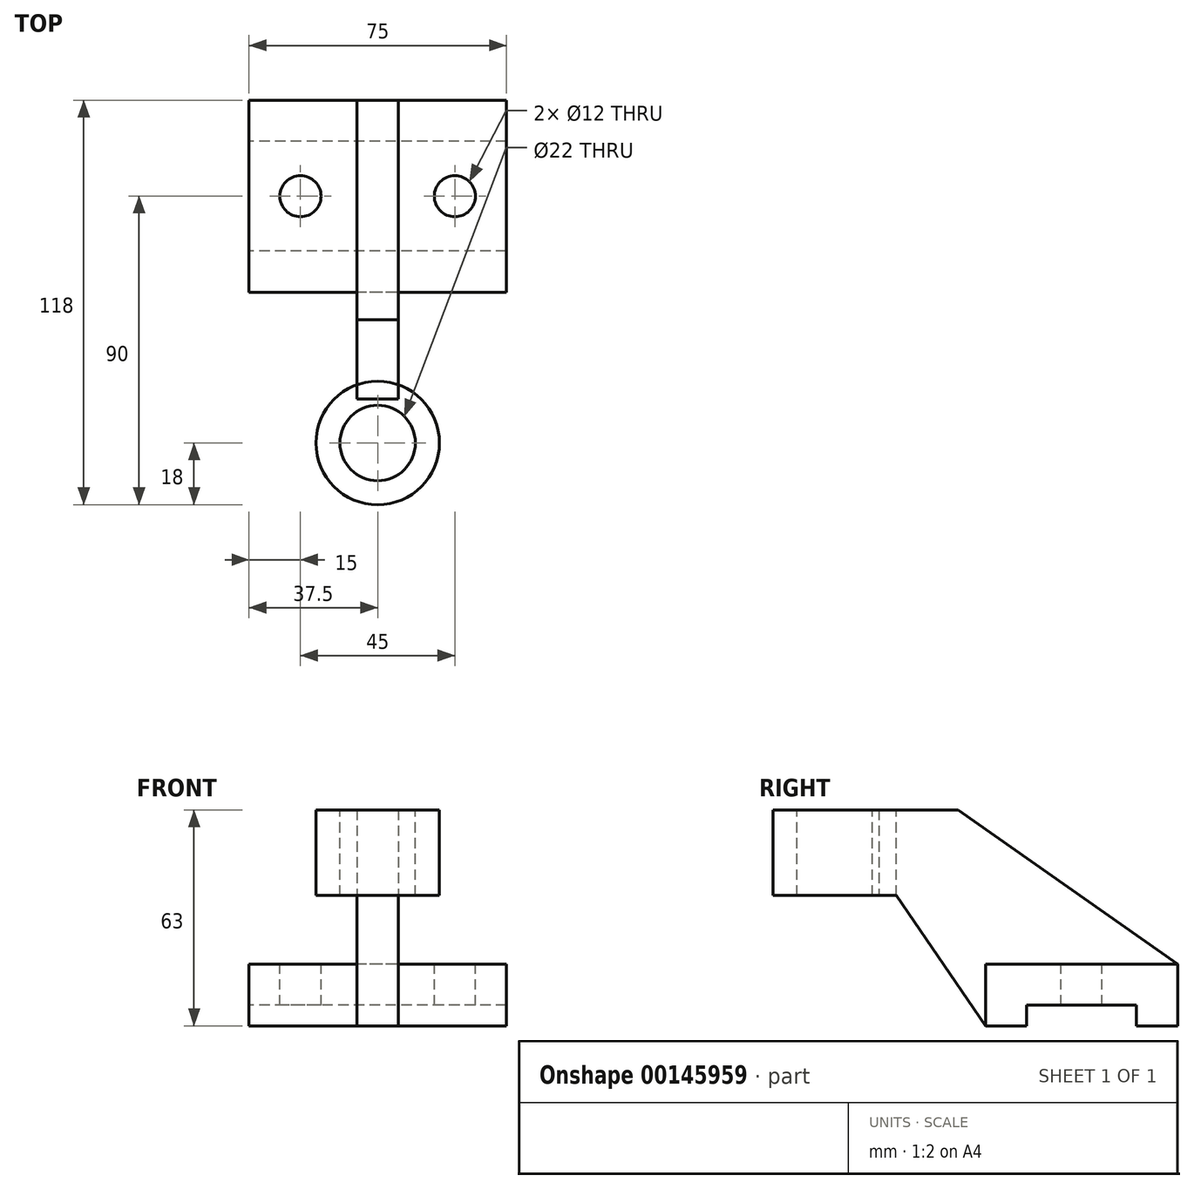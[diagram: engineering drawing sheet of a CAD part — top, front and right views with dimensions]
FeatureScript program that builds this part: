
annotation { "Feature Type Name" : "Feature", "Feature Type Description" : "" }
export const myFeature = defineFeature(function(context is Context, id is Id, definition is map)
    precondition{}
    {
        {
            var Q0;
            Q0=qCreatedBy(makeId("Right.planeOp"),FACE);
            var sketch = newSketch(context, id + "F0", { "sketchPlane" : qUnion([Q0])});
            skLineSegment(sketch, "E0.bottom", {"start": v(-28, 0) * mm, "end": v(-16, 0) * mm});
            skLineSegment(sketch, "E0.top", {"start": v(-28, 18) * mm, "end": v(28, 18) * mm});
            skLineSegment(sketch, "E0.left", {"start": v(-28, 0) * mm, "end": v(-28, 18) * mm});
            skLineSegment(sketch, "E0.right", {"start": v(28, 0) * mm, "end": v(28, 18) * mm});
            skLineSegment(sketch, "E1", {"start": v(-16, 0) * mm, "end": v(-16, 6) * mm});
            skLineSegment(sketch, "E2", {"start": v(-16, 6) * mm, "end": v(16, 6) * mm});
            skLineSegment(sketch, "E3", {"start": v(16, 6) * mm, "end": v(16, 0) * mm});
            skLineSegment(sketch, "E4.trimOffspring", {"start": v(16, 0) * mm, "end": v(28, 0) * mm});
            skSolve(sketch);
        }
        {
            var Q0;
            Q0 = qSketchRegion(id + "F0", true);
            extrude(context, id + "F1", {"entities" : qUnion([Q0]), "endBound" : BoundingType.SYMMETRIC, "depth" : 75 * mm});
        }
        {
            var Q0;
            Q0=makeQuery(id+"F1.opExtrude","SWEPT_FACE",FACE,{"disambiguationData":[OSD([sQuery(id+"F0.wireOp",EDGE,"E0.top")])]});
            var sketch = newSketch(context, id + "F2", { "sketchPlane" : qUnion([Q0])});
            skCircle(sketch, "E5", {"center": v(22.5, 0) * mm, "radius": 6 * mm});
            skCircle(sketch, "E6", {"center": v(-22.5, 0) * mm, "radius": 6 * mm});
            skSolve(sketch);
        }
        {
            var Q0;
            Q0 = qSketchRegion(id + "F2", true);
            extrude(context, id + "F3", {"entities" : qUnion([Q0]), "operationType" : NewBodyOperationType.REMOVE, "oppositeDirection" : true, "depth" : 25 * mm});
        }
        {
            var Q0;
            Q0=qCreatedBy(makeId("Right.planeOp"),FACE);
            var sketch = newSketch(context, id + "F4", { "sketchPlane" : qUnion([Q0])});
            skLineSegment(sketch, "E7.0", {"start": v(28, 0) * mm, "end": v(28, 18) * mm, "construction": true});
            skLineSegment(sketch, "E8.0", {"start": v(-28, 0) * mm, "end": v(-28, 18) * mm, "construction": true});
            skLineSegment(sketch, "E9", {"start": v(28, 18) * mm, "end": v(-36, 63) * mm});
            skLineSegment(sketch, "E10", {"start": v(-36, 63) * mm, "end": v(-72, 63) * mm});
            skSolve(sketch);
        }
        {
            var Q0;
            Q0=qCreatedBy(makeId("Top.planeOp"),FACE);
            cPlane(context, id + "F5", {"entities" : qUnion([Q0]), "cplaneType" : CPlaneType.OFFSET, "offset" : 63 * mm, "width" : 150 * mm, "height" : 150 * mm});
        }
        {
            var Q0;
            Q0=qCreatedBy(id+"F5.planeOp",FACE);
            var sketch = newSketch(context, id + "F6", { "sketchPlane" : qUnion([Q0])});
            skPoint(sketch, "E11.0", {"position": v(0, -72) * mm});
            skCircle(sketch, "E12", {"center": v(0, -72) * mm, "radius": 18 * mm});
            skCircle(sketch, "E13", {"center": v(0, -72) * mm, "radius": 11 * mm});
            skSolve(sketch);
        }
        {
            var Q0;
            Q0 = qSketchRegion(id + "F6", true);
            extrude(context, id + "F7", {"entities" : qUnion([Q0]), "oppositeDirection" : true, "depth" : 25 * mm});
        }
        {
            var Q0;
            Q0=qCreatedBy(makeId("Right.planeOp"),FACE);
            var sketch = newSketch(context, id + "F8", { "sketchPlane" : qUnion([Q0])});
            skPoint(sketch, "E14.0", {"position": v(-28, 18) * mm});
            skPoint(sketch, "E15.0", {"position": v(-72, 63) * mm});
            skPoint(sketch, "E16.0", {"position": v(-36, 63) * mm});
            skPoint(sketch, "E17.0", {"position": v(28, 18) * mm});
            skPoint(sketch, "E18.0", {"position": v(-28, 0) * mm});
            skLineSegment(sketch, "E19", {"start": v(-28, 0) * mm, "end": v(-54, 38) * mm});
            skLineSegment(sketch, "E20", {"start": v(-36, 63) * mm, "end": v(28, 18) * mm});
            skLineSegment(sketch, "E21", {"start": v(-28, 0) * mm, "end": v(-28, 18) * mm});
            skLineSegment(sketch, "E22", {"start": v(-28, 18) * mm, "end": v(28, 18) * mm});
            skPoint(sketch, "E23.start.orphan", {"position": v(-54, 63) * mm});
            skPoint(sketch, "E24.0.end.orphan", {"position": v(-54, 38) * mm});
            skPoint(sketch, "E24.0.start.orphan", {"position": v(-90, 38) * mm});
            skLineSegment(sketch, "E25", {"start": v(-36, 63) * mm, "end": v(-59.14, 63) * mm});
            skLineSegment(sketch, "E26", {"start": v(-59.14, 63) * mm, "end": v(-59.14, 38) * mm});
            skLineSegment(sketch, "E27", {"start": v(-59.14, 38) * mm, "end": v(-54, 38) * mm});
            skSolve(sketch);
        }
        {
            var Q0;
            Q0 = qSketchRegion(id + "F8", true);
            extrude(context, id + "F9", {"entities" : qUnion([Q0]), "endBound" : BoundingType.SYMMETRIC, "depth" : 12 * mm});
        }
    });
